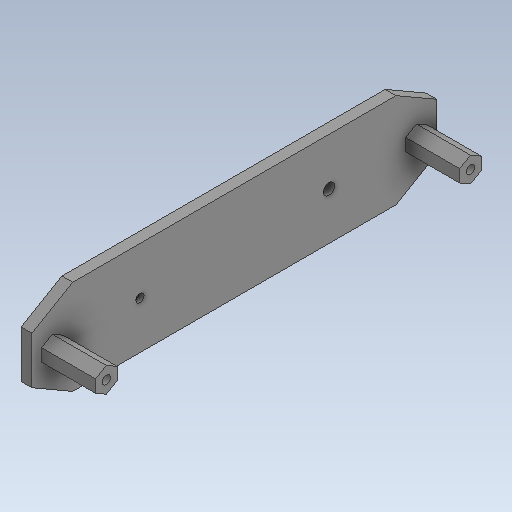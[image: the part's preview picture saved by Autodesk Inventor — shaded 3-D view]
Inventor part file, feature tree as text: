
AUTODESK INVENTOR PART (.ipt)
format: ipt  version: 2020 (Build 240168000, 168)  size: 226,816 bytes
history: native  units: in
note: dims shown in document units (in); Inventor stores cm internally (conversion verified against a paired STEP export)
features: extrude x7, sketch x7, plane x1
ambient origin geometry x8: Origin, YZ Plane, XZ Plane, XY Plane, X Axis, Y Axis, Z Axis, Center Point
bodies: Solid1 (feature_tree)
feature tree (15):
  extrude  "Extrusion1"  Depth=5.9055in
  extrude  "Extrusion3"  TaperAngle=0.0deg  [1 undecoded]
  extrude  "Extrusion4"  Depth=0.7874in
  plane  "Work Plane1"
  extrude  "Extrusion5"  Depth=0.122in
  extrude  "Extrusion6"  Depth=0.2402in
  extrude  "Extrusion7"  [1 undecoded]
  extrude  "Extrusion8"  Depth=0.0866in TaperAngle=0.0deg
  sketch  "Sketch1"  dims[d0=1.378in d1=5.9055in]
  sketch  "Sketch2"  dims[d2=0.1575in d3=0.0in]
  sketch  "Sketch3"  dims[d8=0.315in d9=0.7874in]
  sketch  "Sketch4"  dims[d10=0.0in d12=0.122in]
  sketch  "Sketch5"  dims[d13=0.0in d14=0.0in d15=0.2402in]
  sketch  "Sketch8"  dims[d16=0.0866in d17=-0.2233in]
  sketch  "Sketch9"  dims[d18=-0.3937in d19=0.0866in d20=0.0in d26=1.5748in d27=0.1654in d28=0.122in d29=1.5748in d30=0.0in d31=0.0in d32=0.2402in d33=0.0866in d34=-0.2233in]
note: 2 required parameter values undecoded (feature->parameter linkage not recoverable at this tier; creation-order binding heuristic only, values carry confidence <= 0.55)
